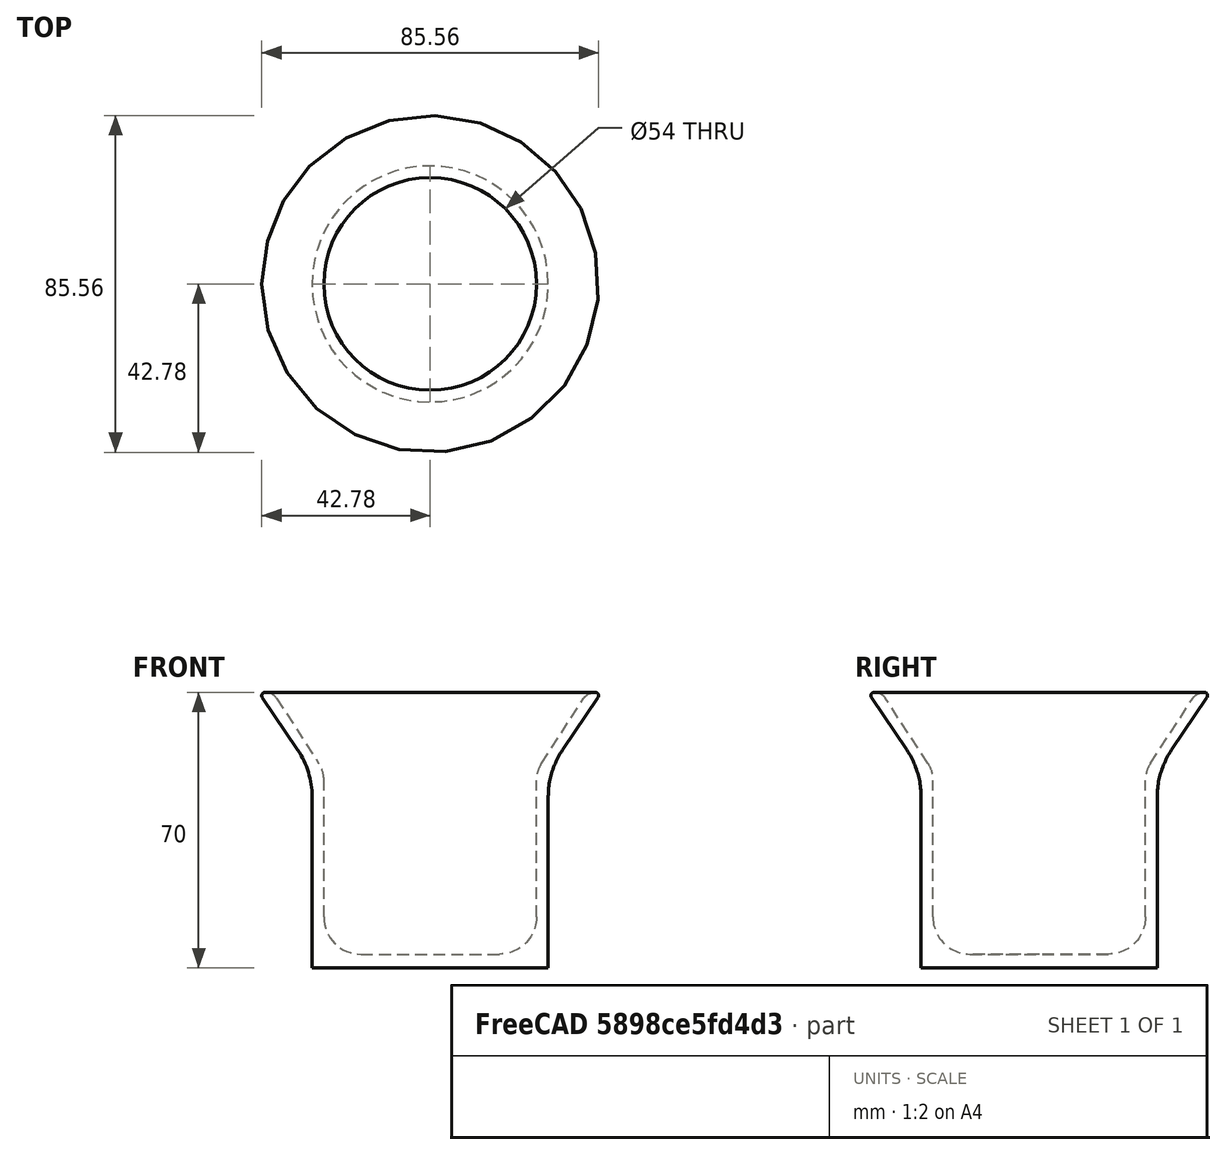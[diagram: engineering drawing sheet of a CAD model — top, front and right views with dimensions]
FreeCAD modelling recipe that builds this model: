
FCSTD DOCUMENT  (FreeCAD 1.1R40607 (Git))
Label: горшок для лука
License: All rights reserved
LicenseURL: https://en.wikipedia.org/wiki/All_rights_reserved
objects: Sketcher::SketchObject×1, PartDesign::Revolution×1, App::Point×1, PartDesign::Body×1
note: 6 computed .brp shape members not serialized (recipe doc carries the construction recipe); baked Part::Feature solids carry a one-line shape summary decoded from their .brp

FEATURE [Sketcher::SketchObject] Sketch
  ArcFitTolerance = 1e-06
  AttachmentSupport = -> [XZ_Plane001]
  ExternalTypes = [0]
  FullyConstrained = false
  MakeInternals = false
  MapMode = 5
  Placement = pos=(0,0,0) rot=(1,0,0;1.5708rad)
  sketch-geometry (18):
    g0: LineSegment StartX=0 StartY=0 StartZ=0 EndX=-30 EndY=0 EndZ=0
    g1: LineSegment StartX=0 StartY=0 StartZ=0 EndX=0 EndY=3.5 EndZ=0
    g2: LineSegment StartX=0 StartY=3.5 StartZ=0 EndX=-17.5894 EndY=3.5 EndZ=0
    g3: LineSegment StartX=-30 StartY=0 StartZ=0 EndX=-30 EndY=43.5187 EndZ=0
    g4: LineSegment StartX=-27 StartY=12.9106 StartZ=0 EndX=-27 EndY=47.6193 EndZ=0
    g5: LineSegment StartX=-33.6261 StartY=55.3721 StartZ=0 EndX=-42.6433 EndY=68.7309 EndZ=0
    g6: LineSegment StartX=-41.9688 StartY=70 StartZ=0 EndX=-41.8155 EndY=70 EndZ=0
    g7: LineSegment StartX=-39.0106 StartY=68.4778 StartZ=0 EndX=-28.2975 EndY=51.9961 EndZ=0
    g8: ArcOfCircle CenterX=-35.031 CenterY=47.6193 CenterZ=0 NormalX=0 NormalY=0 NormalZ=1 AngleXU=0 Radius=8.03098 StartAngle=0 EndAngle=0.576375
    g9: GeomPoint [constr] X=-27 Y=50 Z=0
    g10: ArcOfCircle CenterX=-51.1867 CenterY=43.5187 CenterZ=0 NormalX=0 NormalY=0 NormalZ=1 AngleXU=0 Radius=21.1867 StartAngle=0 EndAngle=0.59375
    g11: GeomPoint [constr] X=-30 Y=50 Z=0
    g12: ArcOfCircle CenterX=-41.9688 CenterY=69.1862 CenterZ=0 NormalX=0 NormalY=0 NormalZ=1 AngleXU=0 Radius=0.813829 StartAngle=1.5708 EndAngle=3.73534
    g13: GeomPoint [constr] X=-43.5 Y=70 Z=0
    g14: ArcOfCircle CenterX=-41.8155 CenterY=66.6545 CenterZ=0 NormalX=0 NormalY=0 NormalZ=1 AngleXU=0 Radius=3.34545 StartAngle=0.576375 EndAngle=1.5708
    g15: GeomPoint [constr] X=-40 Y=70 Z=0
    g16: ArcOfCircle CenterX=-17.5894 CenterY=12.9106 CenterZ=0 NormalX=0 NormalY=0 NormalZ=1 AngleXU=0 Radius=9.41057 StartAngle=3.14159 EndAngle=4.71239
    g17: GeomPoint [constr] X=-27 Y=3.5 Z=0
  constraints (38):
    c: Coincident(g0,g-1)
    c: PointOnObject(g0,g-1)
    c: DistanceX(g0,g0) = 30
    c: Coincident(g1,g0)
    c: PointOnObject(g1,g-2)
    c: Distance(g1,g1) = 3.5
    c: Coincident(g2,g1)
    c: Horizontal(g2)
    c: DistanceX(g17,g2) = 27
    c: Coincident(g3,g0)
    c: Vertical(g3)
    c: Vertical(g4)
    c: Horizontal(g6)
    c: Horizontal(g9,g11)
    c: DistanceY(g3,g11) = 50
    c: DistanceY(g-1,g13) = 70
    c: Distance(g13,g15) = 3.5
    c: Distance(g15,g-2) = 40
    c: PointOnObject(g9,g4)
    c: PointOnObject(g9,g7)
    c: Tangent(g4,g8) = -1.5708
    c: Tangent(g7,g8) = 1.5708
    c: PointOnObject(g11,g3)
    c: PointOnObject(g11,g5)
    c: Tangent(g3,g10) = -1.5708
    c: Tangent(g5,g10) = -1.5708
    c: PointOnObject(g13,g5)
    c: PointOnObject(g13,g6)
    c: Tangent(g5,g12) = 1.5708
    c: Tangent(g6,g12) = 1.5708
    c: PointOnObject(g15,g7)
    c: PointOnObject(g15,g6)
    c: Tangent(g7,g14) = 1.5708
    c: Tangent(g6,g14) = 1.5708
    c: PointOnObject(g17,g4)
    c: PointOnObject(g17,g2)
    c: Tangent(g4,g16) = 1.5708
    c: Tangent(g2,g16) = 1.5708
FEATURE [PartDesign::Revolution] Revolution
  Angle = 360
  Angle2 = 60
  Axis = (0,2e-16,1)
  Base = (0,0,0)
  Placement = pos=(0,0,0) rot=(1,0,0;1.5708rad)
  Profile = -> Sketch
  ReferenceAxis = -> Sketch [V_Axis]
  Refine = true
  Suppressed = false
  Type = 0
FEATURE [App::Point] Origin003  label="Начало координат002"
  Role = Origin
FEATURE [PartDesign::Body] Body
  AllowCompound = false
  Group = -> [Sketch,Revolution]
  Origin = -> Origin002
  Tip = -> Revolution
